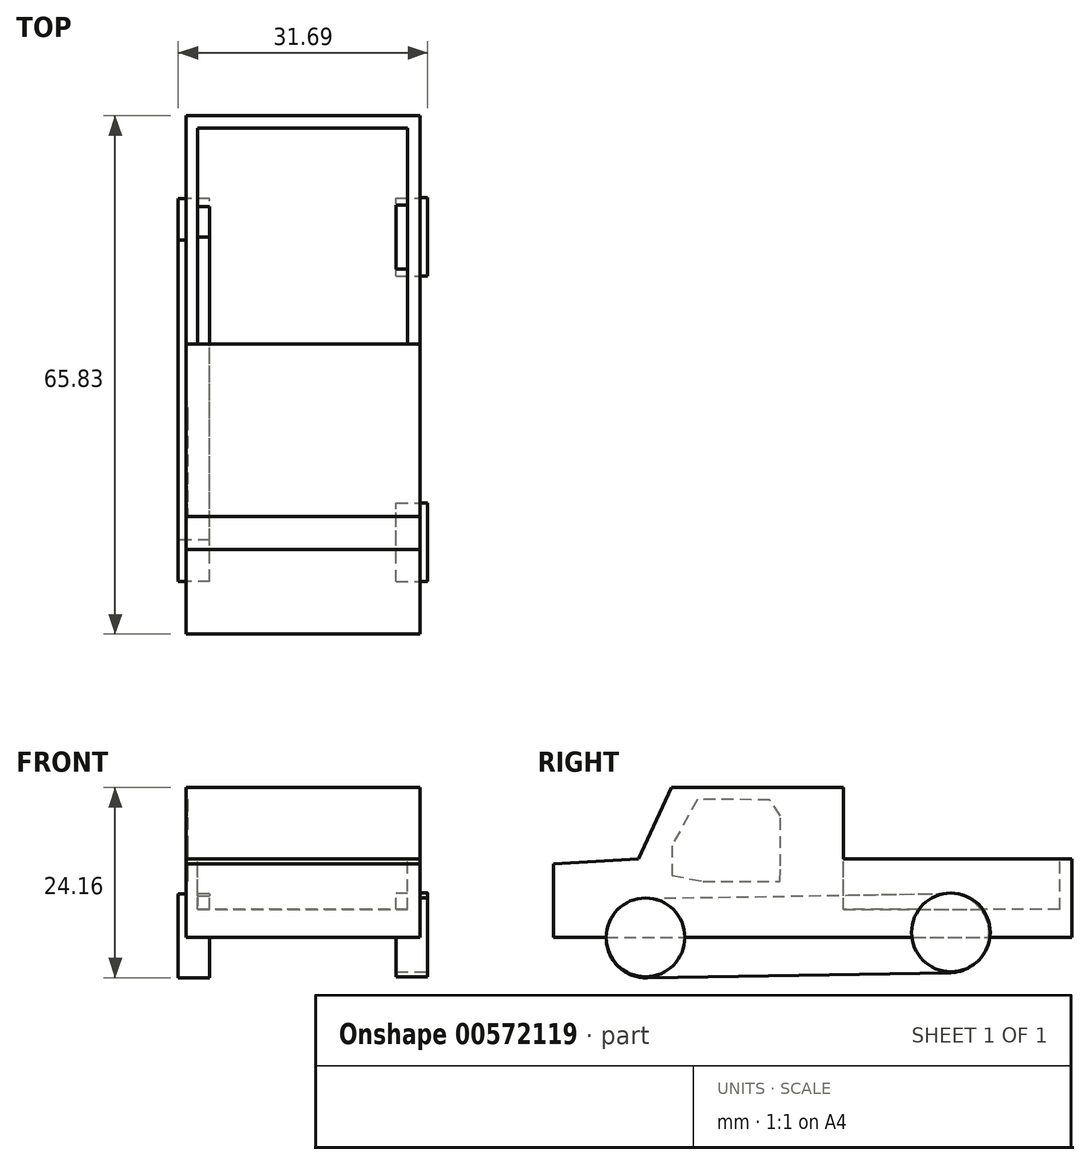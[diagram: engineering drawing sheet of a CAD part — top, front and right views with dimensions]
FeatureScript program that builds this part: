
annotation { "Feature Type Name" : "Feature", "Feature Type Description" : "" }
export const myFeature = defineFeature(function(context is Context, id is Id, definition is map)
    precondition{}
    {
        {
            var Q0;
            Q0=qCreatedBy(makeId("Front.planeOp"),FACE);
            var sketch = newSketch(context, id + "F0", { "sketchPlane" : qUnion([Q0])});
            skLineSegment(sketch, "E0.bottom", {"start": v(0, 0) * mm, "end": v(45.69, 0) * mm});
            skLineSegment(sketch, "E0.top", {"start": v(0, 30.96) * mm, "end": v(45.69, 30.96) * mm});
            skLineSegment(sketch, "E0.left", {"start": v(0, 0) * mm, "end": v(0, 30.96) * mm});
            skLineSegment(sketch, "E0.right", {"start": v(45.69, 0) * mm, "end": v(45.69, 30.96) * mm});
            skSolve(sketch);
        }
        {
            var Q0;
            Q0 = qSketchRegion(id + "F0", true);
            extrude(context, id + "F1", {"entities" : qUnion([Q0]), "depth" : 106 * mm, "offsetDistance" : 25 * mm});
        }
        {
            var Q0;
            Q0=makeQuery(id+"F1.opExtrude","SWEPT_FACE",FACE,{"disambiguationData":[OSD([sQuery(id+"F0.wireOp",EDGE,"E0.left")])]});
            var sketch = newSketch(context, id + "F2", { "sketchPlane" : qUnion([Q0])});
            skLineSegment(sketch, "E1", {"start": v(106, 9.61) * mm, "end": v(40.17, 9.61) * mm});
            skLineSegment(sketch, "E2", {"start": v(69.18, 19.56) * mm, "end": v(40.17, 19.56) * mm});
            skLineSegment(sketch, "E3", {"start": v(40.17, 19.56) * mm, "end": v(40.17, 9.61) * mm});
            skLineSegment(sketch, "E4", {"start": v(69.18, 19.56) * mm, "end": v(69.18, 28.65) * mm});
            skLineSegment(sketch, "E5", {"start": v(69.18, 28.65) * mm, "end": v(91.07, 28.65) * mm});
            skLineSegment(sketch, "E6", {"start": v(91.07, 28.65) * mm, "end": v(95.26, 19.56) * mm});
            skLineSegment(sketch, "E7", {"start": v(95.26, 19.56) * mm, "end": v(106, 18.94) * mm});
            skLineSegment(sketch, "E8", {"start": v(61.87, 19.56) * mm, "end": v(65.58, 19.56) * mm});
            skSolve(sketch);
        }
        {
            var Q0;
            {var subQ5=sQuery(id+"F2.wireOp",EDGE,"E3");Q0=makeQuery(id+"F2.imprint","IMPRINT",FACE,{"disambiguationData":[TD([[makeQuery(id+"F2.imprint","IMPRINT",EDGE,{"derivedFrom":subQ5}),-1.0]])]});}
            extrude(context, id + "F3", {"entities" : qUnion([Q0]), "operationType" : NewBodyOperationType.REMOVE, "oppositeDirection" : true, "depth" : 149 * mm, "offsetDistance" : 25 * mm});
        }
        {
            var Q0;
            Q0=makeQuery(id+"F3.boolean.opBoolean","COPY",FACE,{"derivedFrom":makeQuery(id+"F3.opExtrude","SWEPT_FACE",FACE,{"disambiguationData":[OSD([sQuery(id+"F2.wireOp",EDGE,"E2"),sQuery(id+"F2.wireOp",EDGE,"E8")])]})});
            var sketch = newSketch(context, id + "F4", { "sketchPlane" : qUnion([Q0])});
            skLineSegment(sketch, "E9.bottom", {"start": v(1.45, -41.72) * mm, "end": v(28.15, -41.72) * mm});
            skLineSegment(sketch, "E9.top", {"start": v(1.45, -69.18) * mm, "end": v(28.15, -69.18) * mm});
            skLineSegment(sketch, "E9.left", {"start": v(1.45, -41.72) * mm, "end": v(1.45, -69.18) * mm});
            skLineSegment(sketch, "E9.right", {"start": v(28.15, -41.72) * mm, "end": v(28.15, -69.18) * mm});
            skSolve(sketch);
        }
        {
            var Q0;
            Q0=makeQuery(id+"F4.imprint","IMPRINT",FACE,{"disambiguationData":[TD([[makeQuery(id+"F4.imprint","IMPRINT",EDGE,{"derivedFrom":sQuery(id+"F4.wireOp",EDGE,"E9.bottom")}),-1.0]])]});
            extrude(context, id + "F5", {"entities" : qUnion([Q0]), "operationType" : NewBodyOperationType.REMOVE, "oppositeDirection" : true, "depth" : 6.4 * mm, "offsetDistance" : 25 * mm});
        }
        {
            var Q0;
            Q0=qCreatedBy(makeId("Right.planeOp"),FACE);
            var sketch = newSketch(context, id + "F6", { "sketchPlane" : qUnion([Q0])});
            skCircle(sketch, "E10", {"center": v(-94.33, 9.5) * mm, "radius": 5 * mm});
            skCircle(sketch, "E11", {"center": v(-55.68, 10.13) * mm, "radius": 5 * mm});
            skLineSegment(sketch, "E12", {"start": v(-55.57, 15.13) * mm, "end": v(-94.41, 14.5) * mm});
            skLineSegment(sketch, "E13", {"start": v(-94.41, 14.5) * mm, "end": v(-94.41, 4.5) * mm});
            skLineSegment(sketch, "E14", {"start": v(-94.41, 4.5) * mm, "end": v(-55.6, 5.13) * mm});
            skSolve(sketch);
        }
        {
            var Q0;
            Q0=makeQuery(id+"F1.opExtrude","SWEPT_FACE",FACE,{"disambiguationData":[OSD([sQuery(id+"F0.wireOp",EDGE,"E0.right")])]});
            extrude(context, id + "F7", {"entities" : qUnion([Q0]), "operationType" : NewBodyOperationType.REMOVE, "oppositeDirection" : true, "depth" : 16 * mm, "offsetDistance" : 25 * mm});
        }
        {
            var Q0;
            Q0=makeQuery(id+"F6.imprint","IMPRINT",FACE,{"disambiguationData":[TD([[makeQuery(id+"F6.imprint","IMPRINT",EDGE,{"derivedFrom":sQuery(id+"F6.wireOp",EDGE,"E11")}),1.0]])]});
            var Q1;
            Q1=makeQuery(id+"F6.imprint","IMPRINT",FACE,{"disambiguationData":[TD([[makeQuery(id+"F6.imprint","IMPRINT",EDGE,{"derivedFrom":sQuery(id+"F6.wireOp",EDGE,"E10")}),1.0]])]});
            var Q2;
            {var subQ3=sQuery(id+"F6.wireOp",EDGE,"E14");var subQ5=sQuery(id+"F6.wireOp",EDGE,"E11");var subQ7=makeQuery(id+"F6.imprint","INTERSECT",VERTEX,{"derivedFrom":[subQ5,subQ3]});Q2=makeQuery(id+"F6.imprint","IMPRINT",FACE,{"disambiguationData":[TD([[makeQuery(id+"F6.imprint","IMPRINT",EDGE,{"disambiguationData":[TD([[subQ7,1.0]])],"derivedFrom":subQ5}),-1.0]])]});}
            var Q3;
            {var subQ0=sQuery(id+"F6.wireOp",EDGE,"E13");Q3=makeQuery(id+"F6.imprint","IMPRINT",FACE,{"disambiguationData":[TD([[makeQuery(id+"F6.imprint","IMPRINT",EDGE,{"derivedFrom":subQ0}),1.0]])]});}
            extrude(context, id + "F8", {"entities" : qUnion([Q0, Q1, Q2, Q3]), "operationType" : NewBodyOperationType.ADD, "depth" : 3 * mm, "offsetDistance" : 25 * mm});
        }
        {
            var Q0;
            Q0=makeQuery(id+"F7.boolean.opBoolean","COPY",FACE,{"derivedFrom":makeQuery(id+"F7.opExtrude","CAP_FACE",FACE,{"disambiguationData":[OSD([sQuery(id+"F0.wireOp",EDGE,"E0.right")])],"isStart":false})});
            var sketch = newSketch(context, id + "F9", { "sketchPlane" : qUnion([Q0])});
            skCircle(sketch, "E15", {"center": v(-94.34, 9.61) * mm, "radius": 5 * mm});
            skCircle(sketch, "E16", {"center": v(-55.55, 10.24) * mm, "radius": 5 * mm});
            skSolve(sketch);
        }
        {
            var Q0;
            Q0 = qSketchRegion(id + "F9", true);
            extrude(context, id + "F10", {"entities" : qUnion([Q0]), "operationType" : NewBodyOperationType.ADD, "oppositeDirection" : true, "depth" : 3 * mm, "offsetDistance" : 25 * mm});
        }
        {
            var Q0;
            Q0 = qSketchRegion(id + "F9", true);
            extrude(context, id + "F11", {"entities" : qUnion([Q0]), "operationType" : NewBodyOperationType.ADD, "depth" : 1 * mm, "offsetDistance" : 25 * mm});
        }
        {
            var Q0;
            Q0 = qSketchRegion(id + "F6", true);
            extrude(context, id + "F12", {"entities" : qUnion([Q0]), "operationType" : NewBodyOperationType.ADD, "oppositeDirection" : true, "depth" : 1 * mm, "offsetDistance" : 25 * mm});
        }
        {
            var Q0;
            Q0=makeQuery(id+"F8.boolean.opBoolean","MERGE",FACE,{"derivedFrom":[makeQuery(id+"F1.opExtrude","SWEPT_FACE",FACE,{"disambiguationData":[OSD([sQuery(id+"F0.wireOp",EDGE,"E0.left")])]}),makeQuery(id+"F8.opExtrude","CAP_FACE",FACE,{"disambiguationData":[OSD([sQuery(id+"F6.wireOp",EDGE,"E10")])],"isStart":true}),makeQuery(id+"F8.opExtrude","CAP_FACE",FACE,{"disambiguationData":[OSD([sQuery(id+"F6.wireOp",EDGE,"E11")])],"isStart":true})]});
            var sketch = newSketch(context, id + "F13", { "sketchPlane" : qUnion([Q0])});
            skLineSegment(sketch, "E17", {"start": v(87.75, 27.13) * mm, "end": v(90.99, 21.26) * mm});
            skLineSegment(sketch, "E18", {"start": v(90.99, 21.26) * mm, "end": v(90.99, 17.48) * mm});
            skLineSegment(sketch, "E19", {"start": v(77.22, 18.66) * mm, "end": v(77.22, 27.08) * mm});
            skLineSegment(sketch, "E20", {"start": v(77.22, 27.08) * mm, "end": v(87.75, 27.13) * mm});
            skLineSegment(sketch, "E21", {"start": v(90.99, 17.48) * mm, "end": v(87.03, 16.74) * mm});
            skLineSegment(sketch, "E22", {"start": v(87.03, 16.74) * mm, "end": v(77.24, 16.74) * mm});
            skLineSegment(sketch, "E23", {"start": v(77.24, 16.74) * mm, "end": v(77.22, 18.66) * mm});
            skLineSegment(sketch, "E24", {"start": v(77.22, 25.03) * mm, "end": v(78.57, 27.1) * mm});
            skSolve(sketch);
        }
        {
            var Q0;
            {var subQ4=sQuery(id+"F13.wireOp",EDGE,"E17");Q0=makeQuery(id+"F13.imprint","IMPRINT",FACE,{"disambiguationData":[TD([[makeQuery(id+"F13.imprint","IMPRINT",EDGE,{"derivedFrom":subQ4}),-1.0]])]});}
            extrude(context, id + "F14", {"entities" : qUnion([Q0]), "operationType" : NewBodyOperationType.REMOVE, "oppositeDirection" : true, "depth" : 0.2 * mm, "offsetDistance" : 25 * mm});
        }
    });
